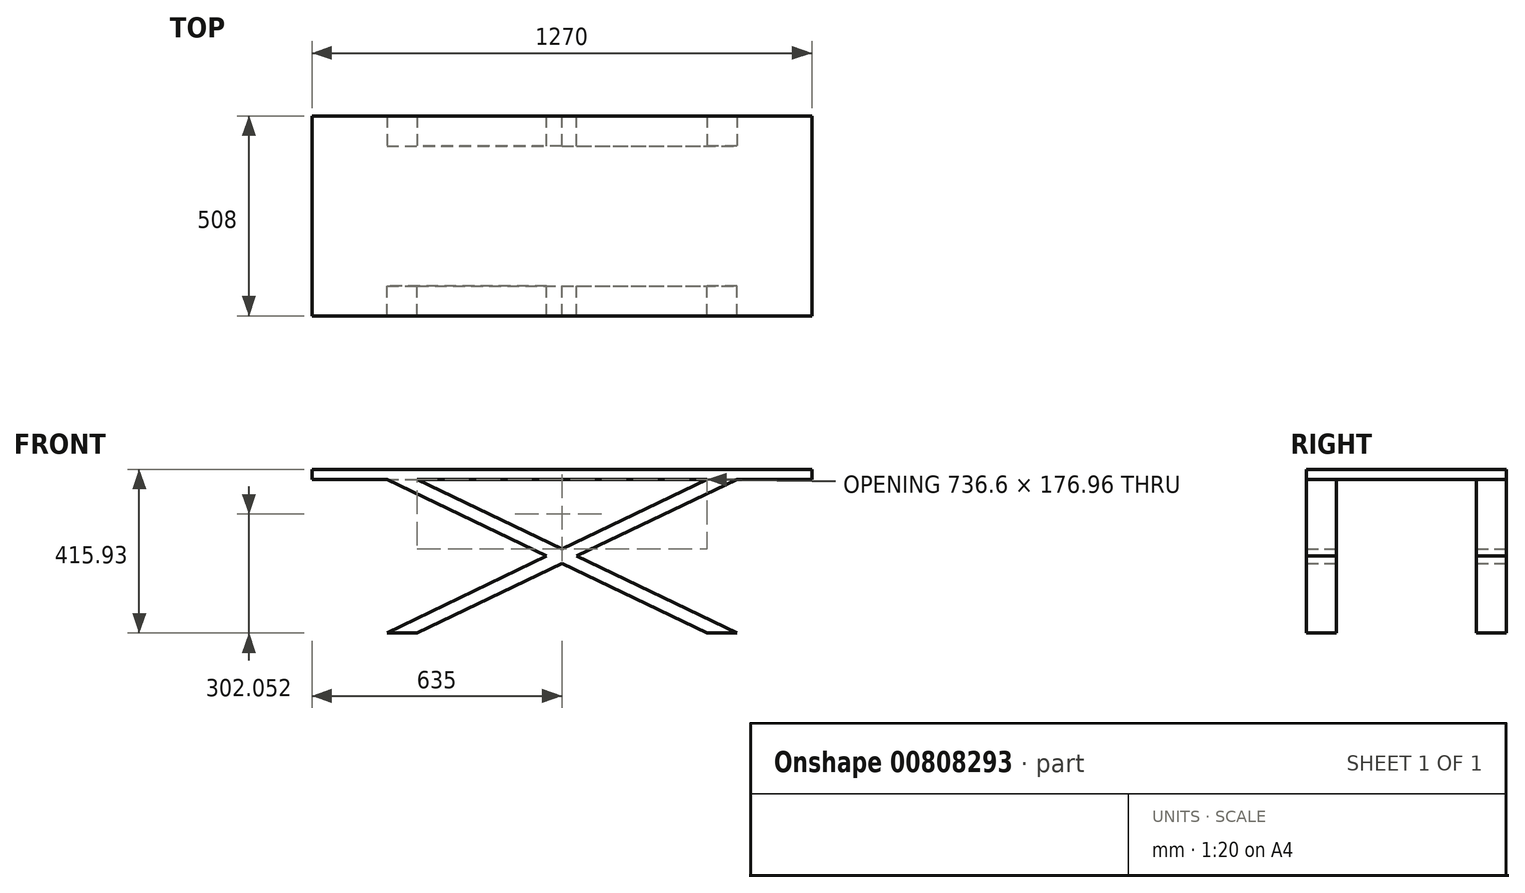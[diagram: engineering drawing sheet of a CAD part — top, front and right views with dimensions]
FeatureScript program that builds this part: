
annotation { "Feature Type Name" : "Feature", "Feature Type Description" : "" }
export const myFeature = defineFeature(function(context is Context, id is Id, definition is map)
    precondition{}
    {
        {
            var Q0;
            Q0=qCreatedBy(makeId("Top.planeOp"),FACE);
            var sketch = newSketch(context, id + "F0", { "sketchPlane" : qUnion([Q0])});
            skLineSegment(sketch, "E0.bottom", {"start": v(635, -254) * mm, "end": v(-635, -254) * mm});
            skLineSegment(sketch, "E0.top", {"start": v(635, 254) * mm, "end": v(-635, 254) * mm});
            skLineSegment(sketch, "E0.left", {"start": v(635, -254) * mm, "end": v(635, 254) * mm});
            skLineSegment(sketch, "E0.right", {"start": v(-635, -254) * mm, "end": v(-635, 254) * mm});
            skPoint(sketch, "E0.middle", {"position": v(0, 0) * mm});
            skSolve(sketch);
        }
        {
            var Q0;
            Q0=qSketchRegion(id+"F0",true);
            extrude(context, id + "F1", {"entities" : qUnion([Q0]), "depth" : 25.4 * mm, "offsetDistance" : 25.4 * mm});
        }
        {
            var Q0;
            Q0=makeQuery(id+"F1.opExtrude","CAP_FACE",FACE,{"disambiguationData":[OSD([sQuery(id+"F0.wireOp",EDGE,"E0.bottom"),sQuery(id+"F0.wireOp",EDGE,"E0.top"),sQuery(id+"F0.wireOp",EDGE,"E0.left"),sQuery(id+"F0.wireOp",EDGE,"E0.right")])],"isStart":true});
            var sketch = newSketch(context, id + "F2", { "sketchPlane" : qUnion([Q0])});
            skLineSegment(sketch, "E1.bottom", {"start": v(-444.5, 254) * mm, "end": v(-368.3, 254) * mm});
            skLineSegment(sketch, "E1.top", {"start": v(-444.5, 177.8) * mm, "end": v(-368.3, 177.8) * mm});
            skLineSegment(sketch, "E1.left", {"start": v(-444.5, 254) * mm, "end": v(-444.5, 177.8) * mm});
            skLineSegment(sketch, "E1.right", {"start": v(-368.3, 254) * mm, "end": v(-368.3, 177.8) * mm});
            skLineSegment(sketch, "E2", {"start": v(0, 254) * mm, "end": v(0, -254) * mm, "construction": true});
            skLineSegment(sketch, "E3", {"start": v(0, 0) * mm, "end": v(-635, 0) * mm, "construction": true});
            skLineSegment(sketch, "E4.MirrorCS", {"start": v(444.5, 177.8) * mm, "end": v(368.3, 177.8) * mm});
            skLineSegment(sketch, "E5.MirrorCS", {"start": v(444.5, 254) * mm, "end": v(444.5, 177.8) * mm});
            skLineSegment(sketch, "E6.MirrorCS", {"start": v(368.3, 254) * mm, "end": v(368.3, 177.8) * mm});
            skLineSegment(sketch, "E7.MirrorCS", {"start": v(444.5, 254) * mm, "end": v(368.3, 254) * mm});
            skLineSegment(sketch, "E8.MirrorCS", {"start": v(-444.5, -177.8) * mm, "end": v(-368.3, -177.8) * mm});
            skLineSegment(sketch, "E9.MirrorCS", {"start": v(-444.5, -254) * mm, "end": v(-368.3, -254) * mm});
            skLineSegment(sketch, "E10.MirrorCS", {"start": v(-444.5, -254) * mm, "end": v(-444.5, -177.8) * mm});
            skLineSegment(sketch, "E11.MirrorCS", {"start": v(-368.3, -254) * mm, "end": v(-368.3, -177.8) * mm});
            skLineSegment(sketch, "E12.MirrorCS", {"start": v(368.3, -254) * mm, "end": v(368.3, -177.8) * mm});
            skLineSegment(sketch, "E13.MirrorCS", {"start": v(444.5, -254) * mm, "end": v(444.5, -177.8) * mm});
            skLineSegment(sketch, "E14.MirrorCS", {"start": v(444.5, -177.8) * mm, "end": v(368.3, -177.8) * mm});
            skLineSegment(sketch, "E15.MirrorCS", {"start": v(444.5, -254) * mm, "end": v(368.3, -254) * mm});
            skSolve(sketch);
        }
        {
            var Q0;
            Q0=makeQuery(id+"F2.imprint","IMPRINT",FACE,{"disambiguationData":[TD([[makeQuery(id+"F2.imprint","IMPRINT",EDGE,{"derivedFrom":sQuery(id+"F2.wireOp",EDGE,"E1.top")}),-1.0]])]});
            cPlane(context, id + "F3", {"entities" : qUnion([Q0]), "cplaneType" : CPlaneType.OFFSET, "offset" : 390.52 * mm, "width" : 152.4 * mm, "height" : 152.4 * mm});
        }
        {
            var Q0;
            Q0=qCreatedBy(id+"F3.planeOp",FACE);
            var sketch = newSketch(context, id + "F4", { "sketchPlane" : qUnion([Q0])});
            skLineSegment(sketch, "E16.0", {"start": v(0, 254) * mm, "end": v(0, -254) * mm});
            skLineSegment(sketch, "E16.1", {"start": v(-368.3, -254) * mm, "end": v(-368.3, -177.8) * mm});
            skLineSegment(sketch, "E16.2", {"start": v(-368.3, 254) * mm, "end": v(-368.3, 177.8) * mm});
            skLineSegment(sketch, "E16.3", {"start": v(444.5, -254) * mm, "end": v(368.3, -254) * mm});
            skLineSegment(sketch, "E16.4", {"start": v(368.3, -254) * mm, "end": v(368.3, -177.8) * mm});
            skLineSegment(sketch, "E16.5", {"start": v(-444.5, -177.8) * mm, "end": v(-368.3, -177.8) * mm});
            skLineSegment(sketch, "E16.6", {"start": v(444.5, 254) * mm, "end": v(368.3, 254) * mm});
            skLineSegment(sketch, "E16.7", {"start": v(444.5, 177.8) * mm, "end": v(368.3, 177.8) * mm});
            skLineSegment(sketch, "E16.8", {"start": v(368.3, 254) * mm, "end": v(368.3, 177.8) * mm});
            skLineSegment(sketch, "E16.9", {"start": v(-444.5, 254) * mm, "end": v(-368.3, 254) * mm});
            skLineSegment(sketch, "E16.10", {"start": v(444.5, -254) * mm, "end": v(444.5, -177.8) * mm});
            skLineSegment(sketch, "E16.11", {"start": v(-444.5, 177.8) * mm, "end": v(-368.3, 177.8) * mm});
            skLineSegment(sketch, "E16.12", {"start": v(-444.5, 254) * mm, "end": v(-444.5, 177.8) * mm});
            skLineSegment(sketch, "E16.13", {"start": v(444.5, -177.8) * mm, "end": v(368.3, -177.8) * mm});
            skLineSegment(sketch, "E16.14", {"start": v(444.5, 254) * mm, "end": v(444.5, 177.8) * mm});
            skLineSegment(sketch, "E16.15", {"start": v(-444.5, -254) * mm, "end": v(-444.5, -177.8) * mm});
            skLineSegment(sketch, "E16.16", {"start": v(-444.5, -254) * mm, "end": v(-368.3, -254) * mm});
            skSolve(sketch);
        }
        {
            var Q1;
            Q1=makeQuery(id+"F2.imprint","IMPRINT",FACE,{"disambiguationData":[TD([[makeQuery(id+"F2.imprint","IMPRINT",EDGE,{"derivedFrom":sQuery(id+"F2.wireOp",EDGE,"E1.bottom")}),1.0]])]});
            var Q2;
            Q2=makeQuery(id+"F4.imprint","IMPRINT",FACE,{"disambiguationData":[TD([[makeQuery(id+"F4.imprint","IMPRINT",EDGE,{"derivedFrom":sQuery(id+"F4.wireOp",EDGE,"E16.6")}),1.0]])]});
            loft(context, id + "F5", {"operationType" : NewBodyOperationType.ADD, "sheetProfilesArray" : [{ "sheetProfileEntities" : qUnion([Q1]) }, { "sheetProfileEntities" : qUnion([Q2]) }]});
        }
        {
            var Q1;
            Q1=makeQuery(id+"F2.imprint","IMPRINT",FACE,{"disambiguationData":[TD([[makeQuery(id+"F2.imprint","IMPRINT",EDGE,{"derivedFrom":sQuery(id+"F2.wireOp",EDGE,"E8.MirrorCS")}),-1.0]])]});
            var Q2;
            Q2=makeQuery(id+"F4.imprint","IMPRINT",FACE,{"disambiguationData":[TD([[makeQuery(id+"F4.imprint","IMPRINT",EDGE,{"derivedFrom":sQuery(id+"F4.wireOp",EDGE,"E16.3")}),-1.0]])]});
            loft(context, id + "F6", {"operationType" : NewBodyOperationType.ADD, "sheetProfilesArray" : [{ "sheetProfileEntities" : qUnion([Q1]) }, { "sheetProfileEntities" : qUnion([Q2]) }]});
        }
        {
            var Q1;
            Q1=makeQuery(id+"F2.imprint","IMPRINT",FACE,{"disambiguationData":[TD([[makeQuery(id+"F2.imprint","IMPRINT",EDGE,{"derivedFrom":sQuery(id+"F2.wireOp",EDGE,"E12.MirrorCS")}),-1.0]])]});
            var Q2;
            Q2=makeQuery(id+"F4.imprint","IMPRINT",FACE,{"disambiguationData":[TD([[makeQuery(id+"F4.imprint","IMPRINT",EDGE,{"derivedFrom":sQuery(id+"F4.wireOp",EDGE,"E16.1")}),1.0]])]});
            loft(context, id + "F7", {"operationType" : NewBodyOperationType.ADD, "sheetProfilesArray" : [{ "sheetProfileEntities" : qUnion([Q1]) }, { "sheetProfileEntities" : qUnion([Q2]) }]});
        }
        {
            var Q1;
            Q1=makeQuery(id+"F2.imprint","IMPRINT",FACE,{"disambiguationData":[TD([[makeQuery(id+"F2.imprint","IMPRINT",EDGE,{"derivedFrom":sQuery(id+"F2.wireOp",EDGE,"E4.MirrorCS")}),-1.0]])]});
            var Q2;
            Q2=makeQuery(id+"F4.imprint","IMPRINT",FACE,{"disambiguationData":[TD([[makeQuery(id+"F4.imprint","IMPRINT",EDGE,{"derivedFrom":sQuery(id+"F4.wireOp",EDGE,"E16.2")}),-1.0]])]});
            loft(context, id + "F8", {"operationType" : NewBodyOperationType.ADD, "sheetProfilesArray" : [{ "sheetProfileEntities" : qUnion([Q1]) }, { "sheetProfileEntities" : qUnion([Q2]) }]});
        }
    });
